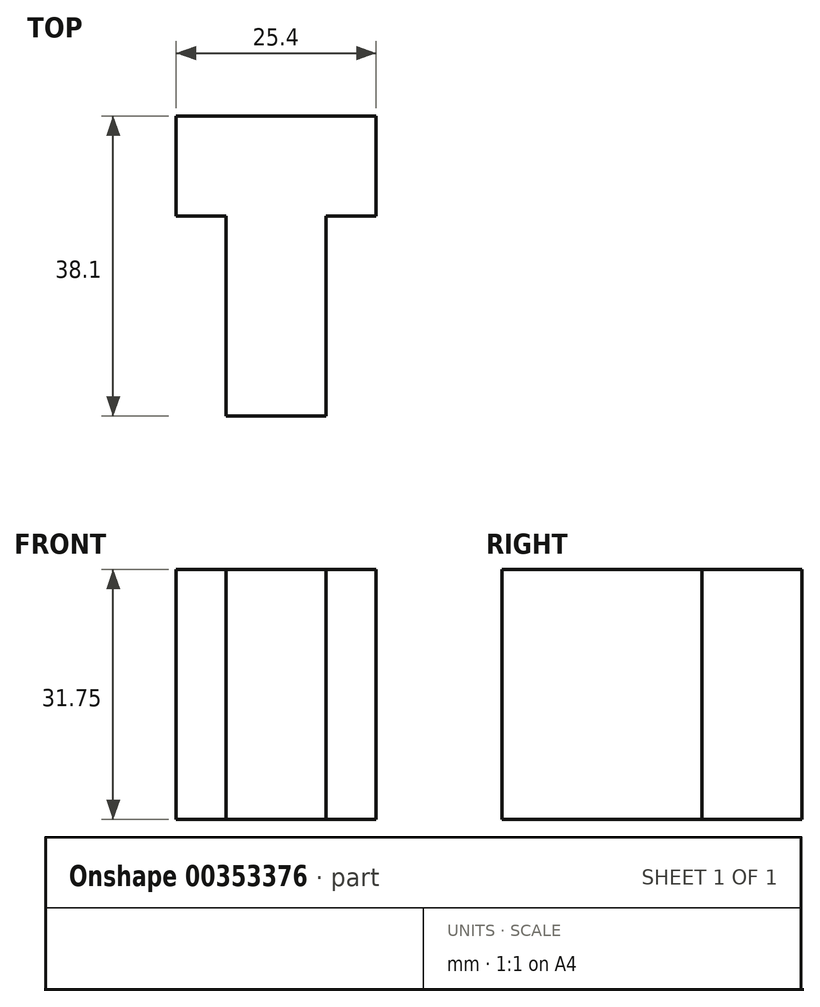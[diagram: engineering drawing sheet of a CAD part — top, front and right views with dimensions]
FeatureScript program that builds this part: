
annotation { "Feature Type Name" : "Feature", "Feature Type Description" : "" }
export const myFeature = defineFeature(function(context is Context, id is Id, definition is map)
    precondition{}
    {
        {
            var Q0;
            Q0=qCreatedBy(makeId("Top.planeOp"),FACE);
            var sketch = newSketch(context, id + "F0", { "sketchPlane" : qUnion([Q0])});
            skLineSegment(sketch, "E0", {"start": v(0, 0) * mm, "end": v(0, 25.4) * mm});
            skLineSegment(sketch, "E1", {"start": v(0, 25.4) * mm, "end": v(-6.35, 25.4) * mm});
            skLineSegment(sketch, "E2", {"start": v(-6.35, 25.4) * mm, "end": v(-6.35, 38.1) * mm});
            skLineSegment(sketch, "E3", {"start": v(-6.35, 38.1) * mm, "end": v(19.05, 38.1) * mm});
            skLineSegment(sketch, "E4", {"start": v(19.05, 38.1) * mm, "end": v(19.05, 25.4) * mm});
            skLineSegment(sketch, "E5", {"start": v(19.05, 25.4) * mm, "end": v(12.7, 25.4) * mm});
            skLineSegment(sketch, "E6", {"start": v(12.7, 25.4) * mm, "end": v(12.7, 0) * mm});
            skLineSegment(sketch, "E7", {"start": v(12.7, 0) * mm, "end": v(0, 0) * mm});
            skSolve(sketch);
        }
        {
            var Q0;
            Q0 = qSketchRegion(id + "F0", true);
            extrude(context, id + "F1", {"entities" : qUnion([Q0]), "depth" : 31.75 * mm});
        }
    });
